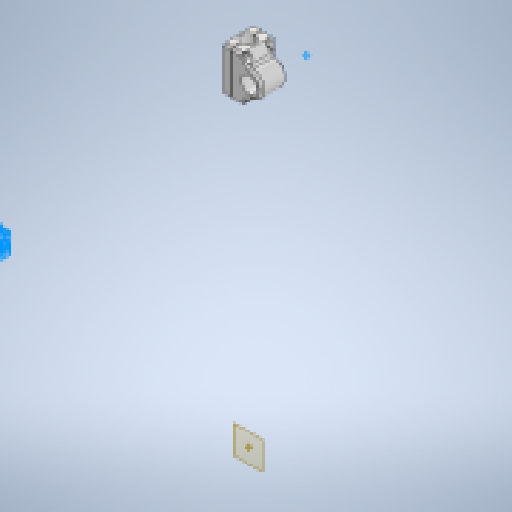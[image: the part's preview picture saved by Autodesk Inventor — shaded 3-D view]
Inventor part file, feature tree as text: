
AUTODESK INVENTOR PART (.ipt)
format: ipt  version: 2024.1 (Build 281209000, 209)  size: 526,336 bytes
history: native  units: mm
features: extrude x11, sketch x11, chamfer x9, other x7, projected_geometry x3, plane x2, fillet x2, reference x2
ambient origin geometry x8: Origin, YZ Plane, XZ Plane, XY Plane, X Axis, Y Axis, Z Axis, Center Point
bodies: Body1 (feature_tree), Body2 (feature_tree), Body3 (feature_tree)
feature tree (47):
  other  "clamp-top"
  plane  "Work Plane1"
  plane  "Work Plane2"
  extrude  "Extrusion1"  Depth=7.5mm
  extrude  "Extrusion2"  Depth=35.0mm TaperAngle=0.0deg
  extrude  "Extrusion3"  Depth=12.3mm
  chamfer  "Chamfer2"  Distance=30.0mm
  extrude  "Extrusion4"  Depth=4.7mm
  chamfer  "Chamfer3"  Distance=2.0mm Angle=45.0deg
  extrude  "Extrusion5"  Depth=3.2mm
  chamfer  "Chamfer4"  Distance=6.0mm
  extrude  "Extrusion7"  Depth=4.0mm
  extrude  "Extrusion6"  Depth=4.0mm
  fillet  "Fillet1"  Radius=3.5mm
  chamfer  "Chamfer9"  [1 undecoded]
  chamfer  "Chamfer10"  Distance=5.45mm
  extrude  "Extrusion8"  Depth=10.0mm TaperAngle=0.0deg
  chamfer  "Chamfer11"  Distance=2.0mm Angle=45.0deg
  chamfer  "Chamfer12"  Distance=6.0mm
  extrude  "Extrusion9"  Depth=4.0mm
  extrude  "Extrusion10"  Depth=4.0mm TaperAngle=45.0deg
  extrude  "Extrusion11"  Depth=4.0mm
  chamfer  "Chamfer13"  Distance=3.0mm
  fillet  "Fillet2"  Radius=0.3mm
  chamfer  "Chamfer1"  Distance=1.0mm
  other  "Work Point1"
  sketch  "Sketch2"  dims[d0=7.5mm d1=7.5mm]
  reference  "Reference1"
  sketch  "Sketch3"  dims[d2=2.0mm d3=35.0mm d4=0.0mm]
  sketch  "Sketch4"  dims[d5=0.25mm d6=12.3mm]
  projected_geometry  "Projected Loop1"
  projected_geometry  "Projected Loop2"
  projected_geometry  "Projected Loop3"
  sketch  "Sketch5"  dims[d7=6.0mm]
  sketch  "Sketch6"  dims[d9=4.0mm d10=30.0mm d11=0.0mm]
  sketch  "Sketch7"  dims[d12=0.0mm d13=0.0mm d14=4.7mm]
  other  "screw-cap"
  sketch  "Sketch8"  dims[d15=4.7mm d16=2.0mm d17=2.0mm d18=45.0deg]
  sketch  "Sketch9"  dims[d19=3.0mm d20=2.0mm d21=45.0deg d22=3.2mm]
  reference  "Reference2"
  other  "clamp-base"
  sketch  "Sketch10"  dims[d23=3.0mm]
  sketch  "Sketch11"  dims[d24=3.0mm]
  sketch  "Sketch12"  dims[d25=6.0mm d26=6.0mm d27=3.0mm d28=3.0mm d29=3.5mm d31=0.0mm d32=0.0mm d33=5.45mm d34=10.0mm d35=0.0mm d36=2.0mm d37=2.0mm d38=45.0deg d39=6.0mm d40=3.5mm d41=2.0mm d42=2.0mm d43=45.0deg d47=5.35mm d48=3.0mm d49=0.0mm d50=0.3mm d51=1.0mm d52=0.0mm d62=2.0mm d63=2.0mm d64=45.0deg d65=1.2mm d66=2.0mm d67=45.0deg d68=0.5mm d69=8.0mm d70=1.0mm d71=0.0mm d72=2.0mm d73=2.0mm d74=45.0deg d75=2.0mm d76=2.0mm d77=45.0deg d78=0.0mm d79=0.0mm d80=4.92mm d81=10.0mm d82=0.0mm d83=35.0mm d84=17.5mm d85=0.0mm d86=0.0mm d87=2.0mm d88=2.0mm d89=45.0deg d90=4.0mm]
  other  "<userpath>\Documents\0004-CAD\3D-cad-main\bike-rack\bike-rack-assembly.iam"
  other  "bike-rack-assembly.iam"
  other  "bike-rack:1"
note: 1 required parameter value undecoded (feature->parameter linkage not recoverable at this tier; creation-order binding heuristic only, values carry confidence <= 0.55)
